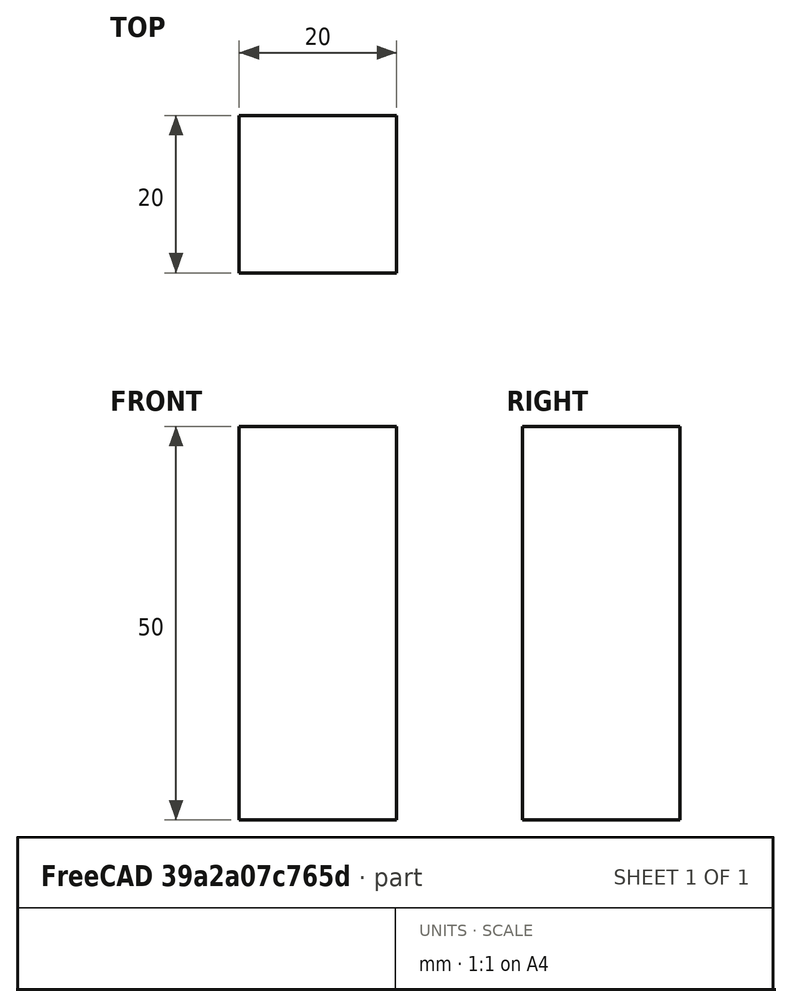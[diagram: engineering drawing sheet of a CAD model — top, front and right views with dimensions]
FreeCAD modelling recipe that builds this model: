
FCSTD DOCUMENT  (FreeCAD 0.15R4671 (Git))
Label: Square Bar 20 EN10059 S235JR
License: All rights reserved
LicenseURL: http://en.wikipedia.org/wiki/All_rights_reserved
objects: Sketcher::SketchObject×1, Part::Extrusion×1
note: 2 computed .brp shape members not serialized (recipe doc carries the construction recipe); baked Part::Feature solids carry a one-line shape summary decoded from their .brp

FEATURE [Sketcher::SketchObject] Sketch
  sketch-geometry (4):
    g0: LineSegment StartX=-10 StartY=-10 StartZ=0 EndX=10 EndY=-10 EndZ=0
    g1: LineSegment StartX=10 StartY=-10 StartZ=0 EndX=10 EndY=10 EndZ=0
    g2: LineSegment StartX=10 StartY=10 StartZ=0 EndX=-10 EndY=10 EndZ=0
    g3: LineSegment StartX=-10 StartY=10 StartZ=0 EndX=-10 EndY=-10 EndZ=0
  constraints (12):
    c: Coincident(g0,g1)
    c: Coincident(g1,g2)
    c: Coincident(g2,g3)
    c: Coincident(g3,g0)
    c: Horizontal(g0)
    c: Horizontal(g2)
    c: Vertical(g1)
    c: Vertical(g3)
    c: Symmetric(g1,g0,g-1)
    c: Symmetric(g2,g1,g-2)
    c: Equal(g1,g2)
    c: DistanceY(g1) = 20
FEATURE [Part::Extrusion] Extrude  label="Square Bar 20 EN10059 S235JR"
  Base = -> Sketch
  Dir = (0,0,50)
  Solid = true
